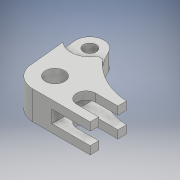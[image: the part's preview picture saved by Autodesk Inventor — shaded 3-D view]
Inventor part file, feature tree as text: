
AUTODESK INVENTOR PART (.ipt)
format: ipt  version: 2018 (Build 220112000, 112)  size: 193,024 bytes
history: native  units: mm
features: extrude x8, sketch x8, chamfer x2
ambient origin geometry x8: Origin, YZ Plane, XZ Plane, XY Plane, X Axis, Y Axis, Z Axis, Center Point
bodies: Solid1 (feature_tree)
feature tree (18):
  extrude  "Extrusion1"  Depth=28.0mm
  extrude  "Extrusion2"  Depth=36.0mm
  extrude  "Extrusion3"  Depth=28.52mm TaperAngle=0.0deg
  extrude  "Extrusion4"  Depth=6.0mm TaperAngle=0.0deg
  extrude  "Extrusion5"  Depth=22.0mm
  extrude  "Extrusion6"  Depth=8.0mm
  extrude  "Extrusion7"  Depth=8.0mm
  extrude  "Extrusion8"  Depth=8.0mm
  chamfer  "Chamfer1"  Distance=12.52mm
  chamfer  "Chamfer2"  Distance=38.0mm
  sketch  "Sketch1"  dims[d0=44.0mm d3=28.0mm]
  sketch  "Sketch2"  dims[d4=57.0mm d5=36.0mm]
  sketch  "Sketch4"  dims[d6=67.0mm d7=28.52mm d8=0.0mm]
  sketch  "Sketch5"  dims[d9=38.0mm d10=6.0mm d11=0.0mm]
  sketch  "Sketch6"  dims[d17=19.05mm d19=22.0mm]
  sketch  "Sketch7"  dims[d20=28.52mm d21=0.0mm d22=8.0mm]
  sketch  "Sketch8"  dims[d23=8.0mm d24=8.0mm]
  sketch  "Sketch9"  dims[d25=0.0mm d26=8.0mm d27=12.52mm d28=38.0mm d29=0.0mm d30=38.0mm d31=0.0mm d32=19.08mm d33=38.0mm d34=0.0mm d36=38.0mm d37=6.0mm d38=0.0mm d39=12.75mm d40=16.52mm d41=0.0mm d51=5.0mm d52=2.0mm d53=20.594885mm d54=5.0mm d55=2.0mm d56=20.594885mm]
